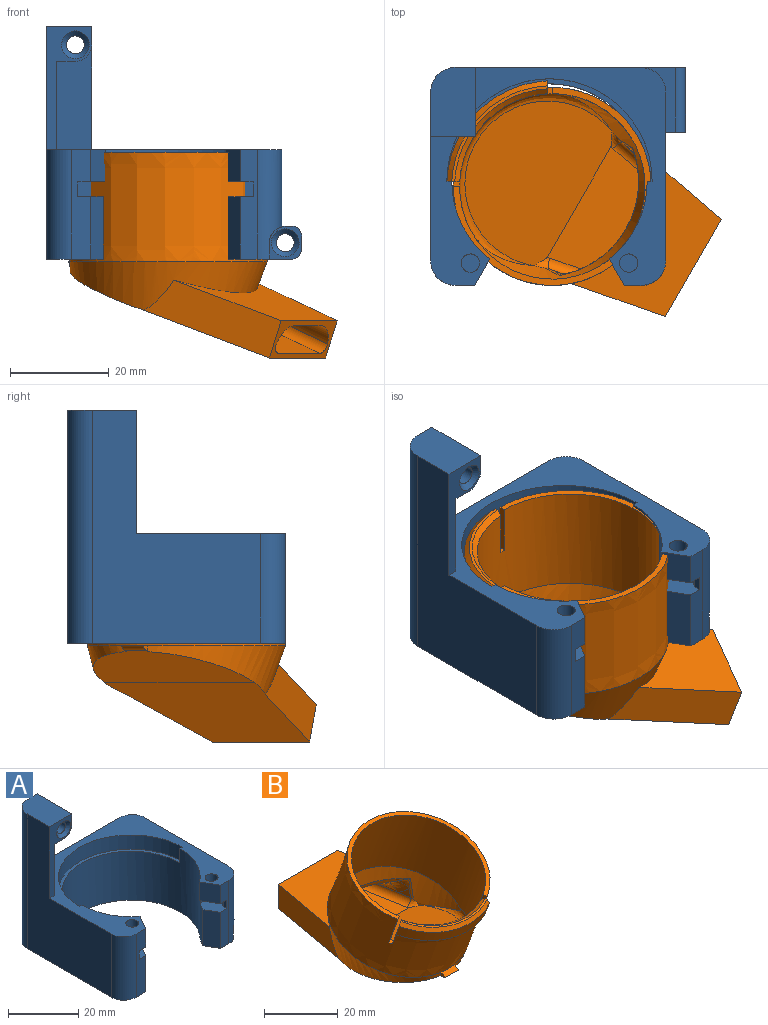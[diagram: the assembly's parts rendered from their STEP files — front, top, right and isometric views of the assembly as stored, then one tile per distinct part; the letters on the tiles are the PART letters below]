
ASSEMBLY  parts=2 mates=1
PART A: 54 faces, bbox 51.5x44x47.1 mm
  f0: plane 3.32x3mm, normal (0,-1,0), area 9.9mm2, adj f1,f8,f31,f51
  f1: plane 3x3mm, normal (-0.87,-0.5,0), area 10.4mm2, adj f0,f2,f31,f51
  f2: plane 3x3mm, normal (-0.87,0.5,0), area 10.4mm2, adj f1,f31,f33,f51
  f3: plane 3x3mm, normal (0.87,-0.5,0), area 10.4mm2, adj f4,f5,f30,f48
  f4: plane 3.32x3mm, normal (0,-1,0), area 9.9mm2, adj f3,f8,f30,f48
  f5: plane 3x3mm, normal (0.87,0.5,0), area 10.4mm2, adj f3,f30,f32,f48
  f6: plane 6.5x5.35mm, normal (-0.87,-0.5,0), area 40.1mm2, adj f8,f11,f19,f31
  f7: plane 6.5x5.35mm, normal (0.87,-0.5,0), area 40.1mm2, adj f8,f14,f19,f30
  f8: cylinder r=19.75mm len=39.5mm, axis (0,0,-1), area 1773.1mm2, adj f0,f4,f6,f7,f15,f19,f30,f31
  f9: plane 21.2x7.1mm, normal (0,-1,0), area 129.4mm2, adj f19,f21,f22,f25,f29
  f10: plane 47.1x46.5mm, normal (0,1,0), area 971.3mm2, adj f15,f19,f23,f25,f27,f28,f34,f37
  f11: plane 22.1x3.37mm, normal (0,-1,0), area 66.6mm2, adj f6,f15,f19,f31,f33,f47,f51,f53
  f12: plane 6.65x6.55mm, normal (0,-1,0), area 14.7mm2, adj f13,f15,f18,f26,f34,f35,f37,f38
  f13: cylinder r=3.25mm len=30.36mm, axis (0,-1,0), area 129.8mm2, adj f12,f18,f26,f47
  f14: plane 22.1x3.87mm, normal (0,-1,0), area 77.6mm2, adj f7,f15,f19,f30,f32,f45,f48,f50
  f15: plane 49.5x44mm, normal (0,0,-1), area 719.8mm2, adj f8,f10,f11,f12,f14,f24,f26,f39
  f16: cylinder r=1.85mm len=6.5mm, axis (0,0,1), area 75.6mm2, adj f19,f30
  f17: cylinder r=1.85mm len=6.5mm, axis (0,0,1), area 75.6mm2, adj f19,f31
  f18: plane 34x15.63mm, normal (1,0,0), area 529.9mm2, adj f12,f13,f19,f37,f44,f47
  f19: plane 47.5x44mm, normal (0,0,1), area 643.1mm2, adj f6,f7,f8,f9,f10,f11,f14,f16
  f20: plane 25x9.1mm, normal (0,-1,0), area 73.4mm2, adj f19,f21,f22,f23,f24,f25,f29,f36
  f21: plane 12x3.8mm, normal (0,0,-1), area 45.6mm2, adj f9,f20,f22,f29
  f22: cylinder r=3.3mm len=12mm, axis (0,1,0), area 62.2mm2, adj f9,f20,f21,f25
  f23: plane 14x9.1mm, normal (0,0,1), area 122mm2, adj f10,f20,f24,f25,f46
  f24: plane 47.1x34mm, normal (-1,0,0), area 976.4mm2, adj f15,f19,f20,f23,f45,f46
  f25: plane 25x14mm, normal (1,0,0), area 95.6mm2, adj f9,f10,f19,f20,f22,f23
  f26: plane 30.36x3.3mm, normal (1,0,0), area 100.2mm2, adj f12,f13,f15,f47
  f27: cylinder r=1.8mm len=12mm, axis (0,-1,0), area 135.7mm2, adj f10,f35
  f28: cylinder r=1.8mm len=13mm, axis (0,-1,0), area 146.8mm2, adj f10,f36,f46
  f29: plane 17.9x12mm, normal (1,0,0), area 214.8mm2, adj f9,f19,f20,f21
  f30: plane 7.5x7.42mm, normal (0,0,-1), area 26.1mm2, adj f3,f4,f5,f7,f8,f14,f16,f32
  f31: plane 7.5x7.42mm, normal (0,0,-1), area 26.1mm2, adj f0,f1,f2,f6,f8,f11,f17,f33
  f32: plane 3x1.5mm, normal (1,0,0), area 4.5mm2, adj f5,f14,f30,f48
  f33: plane 3x1.5mm, normal (-1,0,0), area 4.5mm2, adj f2,f11,f31,f51
  f34: plane 13x2.65mm, normal (1,0,0), area 34.4mm2, adj f10,f12,f38,f39
  f35: cone r=1.8mm half-angle=45deg, axis (0,-1,0), area 20.4mm2, adj f12,f27
  f36: cone r=1.8mm half-angle=45deg, axis (0,-1,0), area 20.4mm2, adj f20,f28
  f37: plane 13x7mm, normal (0,0,1), area 31.4mm2, adj f10,f12,f18,f38,f44
  f38: cylinder r=2mm len=13mm, axis (0,-1,0), area 40.8mm2, adj f10,f12,f34,f37
  f39: cylinder r=2mm len=13mm, axis (0,1,0), area 40.8mm2, adj f10,f12,f15,f34
  f40: plane 5x1mm, normal (0,1,0), area 5mm2, adj f8,f19,f42,f43
  f41: plane 5x1mm, normal (0,1,0), area 5mm2, adj f8,f19,f42,f43
  f42: cylinder r=20.75mm len=41.5mm, axis (0,0,-1), area 325.9mm2, adj f19,f40,f41,f43
  f43: plane 41.5x20.75mm, normal (0,0,1), area 63.6mm2, adj f8,f40,f41,f42
  f44: cylinder r=5mm len=15.45mm, axis (0,0,1), area 121.3mm2, adj f10,f18,f19,f37
  f45: cylinder r=5mm len=22.1mm, axis (0,0,1), area 173.6mm2, adj f14,f15,f19,f24
  f46: cylinder r=5mm len=47.1mm, axis (0,0,-1), area 367.6mm2, adj f10,f15,f23,f24,f28
  f47: cylinder r=5mm len=22.1mm, axis (0,0,-1), area 142.1mm2, adj f11,f13,f15,f18,f19,f26
  f48: plane 7.5x6.93mm, normal (0,0,1), area 35.7mm2, adj f3,f4,f5,f8,f14,f32,f49,f50
  f49: plane 12.6x2.62mm, normal (0.87,0.5,0), area 38.1mm2, adj f8,f15,f48,f50
  f50: plane 12.6x4.5mm, normal (0.87,-0.5,0), area 65.5mm2, adj f14,f15,f48,f49
  f51: plane 7.5x6.93mm, normal (0,0,1), area 35.7mm2, adj f0,f1,f2,f8,f11,f33,f52,f53
  f52: plane 12.6x2.62mm, normal (-0.87,0.5,0), area 38.1mm2, adj f8,f15,f51,f53
  f53: plane 12.6x4.5mm, normal (-0.87,-0.5,0), area 65.5mm2, adj f11,f15,f51,f52
PART B: 47 faces, bbox 40.3x63.4x35.9 mm
  f0: extruded ~45.15x40mm, area 2624.8mm2, adj f1,f4,f13,f19,f20,f21,f22,f23
  f1: plane 40x35.08mm, normal (0,-0.34,0.94), area 114.1mm2, adj f0,f3,f21,f22
  f2: plane 26.4x9.04mm, normal (0,-0.34,0.94), area 17.7mm2, adj f19,f24,f25,f26
  f3: cylinder r=18.75mm len=42.8mm, axis (0,-0.34,0.94), area 2350.6mm2, adj f1,f15,f19,f20,f21,f22,f23,f24
  f4: plane 27.77x9.87mm, normal (0,0.34,-0.94), area 41.1mm2, adj f0,f5,f19,f24
  f5: cylinder r=21.35mm len=27.77mm, axis (0,-0.34,0.94), area 110.4mm2, adj f4,f19,f24,f25
  f6: plane 33.5x27.75mm, normal (0,0.21,0.98), area 795.2mm2, adj f14,f27,f32,f34
  f7: plane 35x35mm, normal (0,0,-1), area 1011.7mm2, adj f8,f9,f10,f12,f13
  f8: plane 22.91x8.26mm, normal (0,1,0), area 69.1mm2, adj f7,f9,f10,f11,f14,f16,f31,f33
  f9: plane 28.3x8mm, normal (-0.98,0.17,0), area 209.1mm2, adj f7,f8,f11,f13
  f10: plane 28.3x8mm, normal (0.98,0.17,0), area 209.1mm2, adj f7,f8,f11,f13
  f11: plane 31.16x24.1mm, normal (0,0,1), area 479.8mm2, adj f8,f9,f10,f13
  f12: plane 35x19.24mm, normal (0,0,-1), area 513.7mm2, adj f7,f13,f43,f44,f46
  f13: bspline ~40x37.59mm, area 647.6mm2, adj f0,f7,f9,f10,f11,f12,f43,f44
  f14: plane 25.81x25.79mm, normal (0,0,1), area 545.7mm2, adj f6,f8,f31,f32,f33,f34
  f15: bspline ~37.47x24.79mm, area 359.3mm2, adj f3,f27,f28,f29,f30,f32,f34
  f16: plane 16.84x16.65mm, normal (0,0,-1), area 210mm2, adj f8,f29,f35,f39
  f17: plane 4.44x2.8mm, normal (-0.98,-0.17,0), area 5.4mm2, adj f30,f33,f41
  f18: plane 4.44x2.8mm, normal (0.98,-0.17,0), area 5.4mm2, adj f28,f31,f37
  f19: plane 9.47x5.2mm, normal (0.87,0.47,0.17), area 17.6mm2, adj f0,f2,f3,f4,f5,f20,f25,f26
  f20: plane 1.51x1.47mm, normal (0,-0.34,0.94), area 1.3mm2, adj f0,f3,f19,f21
  f21: plane 9.77x4.44mm, normal (-0.87,-0.47,-0.17), area 12.5mm2, adj f0,f1,f3,f20
  f22: plane 9.61x4.01mm, normal (0.5,-0.81,-0.3), area 12.5mm2, adj f0,f1,f3,f23
  f23: plane 1.61x1.39mm, normal (0,-0.34,0.94), area 1.3mm2, adj f0,f3,f22,f24
  f24: plane 9.44x4.3mm, normal (-0.5,0.81,0.3), area 17.6mm2, adj f0,f2,f3,f4,f5,f23,f25,f26
  f25: cone r=21.35mm half-angle=45deg, axis (0,0.34,-0.94), area 43.5mm2, adj f2,f5,f19,f24
  f26: cone r=18.75mm half-angle=45deg, axis (0,-0.34,0.94), area 39.9mm2, adj f2,f3,f19,f24
  f27: bspline ~37.48x28.73mm, area 134.3mm2, adj f3,f6,f15,f32,f34
  f28: bspline ~9.29x2.45mm, area 3.8mm2, adj f15,f18,f32,f38
  f29: bspline ~34.8x10.95mm, area 77mm2, adj f15,f16,f36,f37,f38,f40,f41,f42
  f30: bspline ~9.29x2.45mm, area 3.8mm2, adj f15,f17,f34,f42
  f31: cylinder r=2mm len=25.57mm, axis (0.17,0.98,0), area 79.9mm2, adj f8,f14,f18,f32,f35,f36
  f32: bspline ~4.23x3.47mm, area 5mm2, adj f6,f14,f15,f27,f28,f31
  f33: cylinder r=2mm len=25.57mm, axis (0.17,-0.98,0), area 79.9mm2, adj f8,f14,f17,f34,f39,f40
  f34: bspline ~4.24x3.47mm, area 5mm2, adj f6,f14,f15,f27,f30,f33
  f35: cylinder r=5mm len=17.69mm, axis (0.17,0.98,0), area 114.1mm2, adj f8,f16,f31,f36
  f36: bspline ~6.14x5.99mm, area 20.9mm2, adj f29,f31,f35,f37
  f37: bspline ~6.42x5.63mm, area 19mm2, adj f18,f29,f36,f38
  f38: bspline ~3.34x2.74mm, area 3.6mm2, adj f28,f29,f37
  f39: cylinder r=5mm len=17.69mm, axis (-0.17,0.98,0), area 114.1mm2, adj f8,f16,f33,f40
  f40: bspline ~6x5.79mm, area 20.9mm2, adj f29,f33,f39,f41
  f41: bspline ~6.42x5.63mm, area 19mm2, adj f17,f29,f40,f42
  f42: bspline ~3.34x2.74mm, area 3.6mm2, adj f29,f30,f41
  f43: plane 2.21x1.2mm, normal (-1,0,0), area 1.6mm2, adj f12,f13,f45,f46
  f44: plane 2.21x1.2mm, normal (1,0,0), area 1.6mm2, adj f12,f13,f45,f46
  f45: plane 5x1.92mm, normal (0,-0.34,0.94), area 9.6mm2, adj f13,f43,f44,f46
  f46: cylinder r=2mm len=5mm, axis (-1,0,0), area 7.1mm2, adj f12,f43,f44,f45
PLACE A rot(axis=(-0.04,0.04,1),0deg) t=(1.83,-76.89,-39.09)mm
PLACE B rot(axis=(-0.1,0.17,-0.98),121deg) t=(20.04,-99.52,-48.61)mm
MATE planar A.f43 <-> B.f4  axis (0,0,1) through (1.08,-99.89,-23.49)mm
